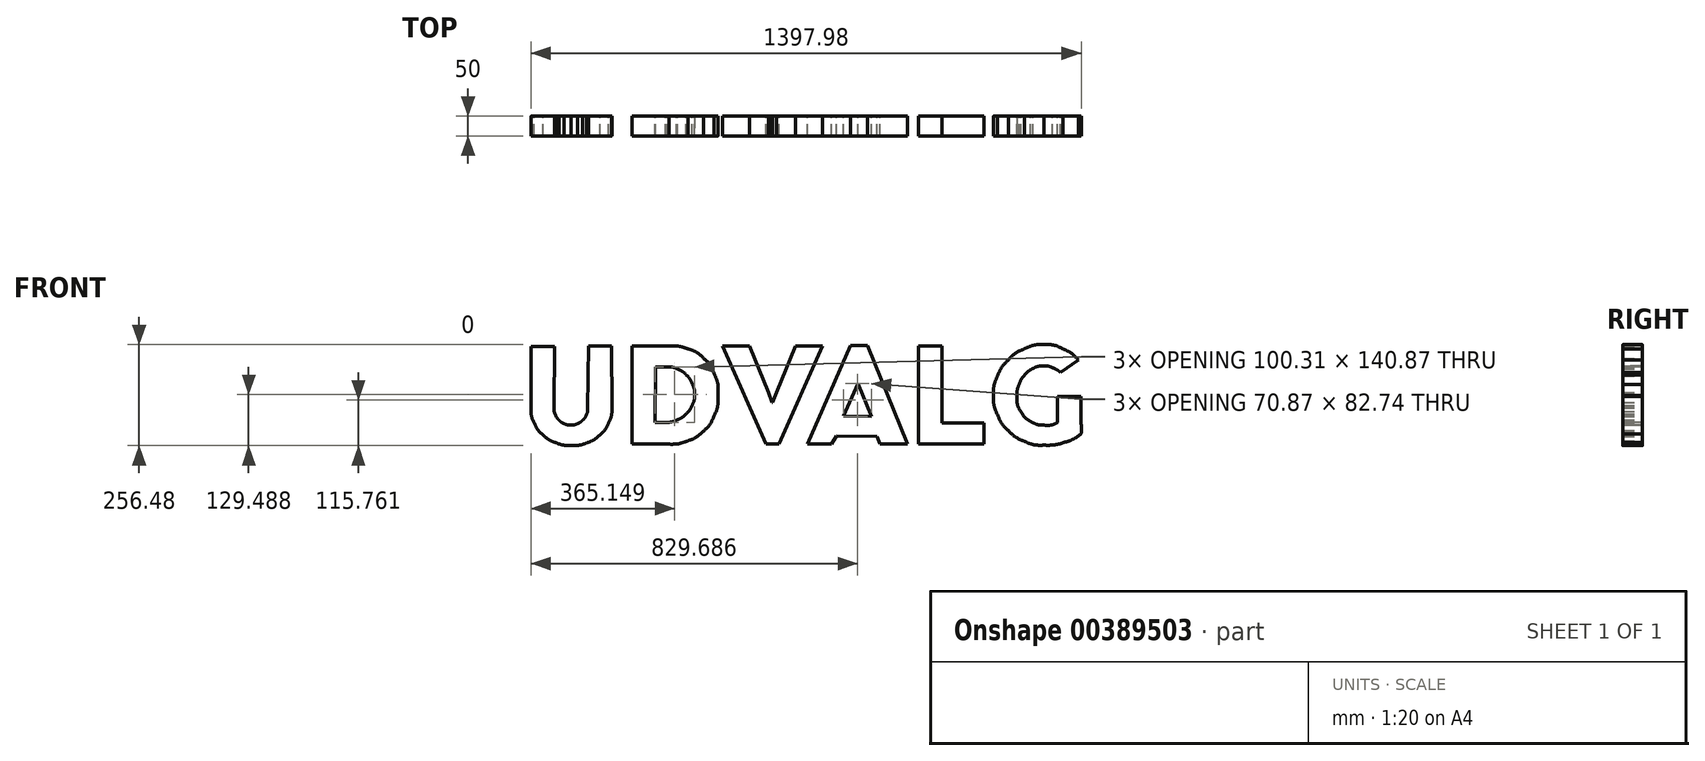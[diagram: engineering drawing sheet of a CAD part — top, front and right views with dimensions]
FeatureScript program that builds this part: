
annotation { "Feature Type Name" : "Feature", "Feature Type Description" : "" }
export const myFeature = defineFeature(function(context is Context, id is Id, definition is map)
    precondition{}
    {
        {
            var Q0;
            Q0=qCreatedBy(makeId("Front.planeOp"),FACE);
            var sketch = newSketch(context, id + "F0", { "sketchPlane" : qUnion([Q0])});
            skFitSpline(sketch, "E0", {"points": [v(-493.53, -31.17) * mm, v(-493.53, -45.27) * mm, v(-496.25, -58.25) * mm, v(-501.7, -70.12) * mm]});
            skFitSpline(sketch, "E1", {"points": [v(-501.7, -70.12) * mm, v(-506.89, -82) * mm, v(-514.18, -92.26) * mm, v(-523.58, -100.92) * mm]});
            skFitSpline(sketch, "E2", {"points": [v(-523.58, -100.92) * mm, v(-532.74, -109.33) * mm, v(-543.62, -116) * mm, v(-556.23, -120.95) * mm]});
            skFitSpline(sketch, "E3", {"points": [v(-556.23, -120.95) * mm, v(-568.6, -125.65) * mm, v(-581.83, -128) * mm, v(-595.93, -128) * mm]});
            skFitSpline(sketch, "E4", {"points": [v(-595.93, -128) * mm, v(-610.03, -128) * mm, v(-623.39, -125.65) * mm, v(-636, -120.95) * mm]});
            skFitSpline(sketch, "E5", {"points": [v(-636, -120.95) * mm, v(-648.37, -116.25) * mm, v(-659.25, -109.7) * mm, v(-668.65, -101.29) * mm]});
            skFitSpline(sketch, "E6", {"points": [v(-668.65, -101.29) * mm, v(-677.8, -92.88) * mm, v(-685.1, -82.86) * mm, v(-690.54, -71.24) * mm]});
            skFitSpline(sketch, "E7", {"points": [v(-690.54, -71.24) * mm, v(-695.99, -59.36) * mm, v(-698.7, -46.38) * mm, v(-698.7, -32.28) * mm]});
            skLineSegment(sketch, "E8", {"start": v(-553.27, 125.04) * mm, "end": v(-493.9, 125.04) * mm});
            skLineSegment(sketch, "E9", {"start": v(-493.9, 125.04) * mm, "end": v(-493.53, -31.17) * mm});
            skFitSpline(sketch, "E10", {"points": [v(-640.46, -33.02) * mm, v(-640.46, -38.96) * mm, v(-639.34, -44.52) * mm, v(-637.12, -49.72) * mm]});
            skFitSpline(sketch, "E11", {"points": [v(-637.12, -49.72) * mm, v(-634.9, -54.91) * mm, v(-631.8, -59.49) * mm, v(-627.84, -63.45) * mm]});
            skFitSpline(sketch, "E12", {"points": [v(-627.84, -63.45) * mm, v(-623.88, -67.4) * mm, v(-619.43, -70.5) * mm, v(-614.48, -72.72) * mm]});
            skFitSpline(sketch, "E13", {"points": [v(-614.48, -72.72) * mm, v(-609.29, -74.95) * mm, v(-603.72, -76.06) * mm, v(-597.79, -76.06) * mm]});
            skFitSpline(sketch, "E14", {"points": [v(-597.79, -76.06) * mm, v(-591.85, -76.06) * mm, v(-586.29, -74.95) * mm, v(-581.1, -72.72) * mm]});
            skFitSpline(sketch, "E15", {"points": [v(-581.1, -72.72) * mm, v(-575.9, -70.5) * mm, v(-571.32, -67.4) * mm, v(-567.36, -63.45) * mm]});
            skFitSpline(sketch, "E16", {"points": [v(-567.36, -63.45) * mm, v(-563.4, -59.49) * mm, v(-560.31, -54.91) * mm, v(-558.09, -49.72) * mm]});
            skFitSpline(sketch, "E17", {"points": [v(-558.09, -49.72) * mm, v(-555.86, -44.52) * mm, v(-554.75, -38.96) * mm, v(-554.75, -33.02) * mm]});
            skLineSegment(sketch, "E18", {"start": v(-698.7, -32.28) * mm, "end": v(-698.7, 123.92) * mm});
            skLineSegment(sketch, "E19", {"start": v(-698.7, 123.92) * mm, "end": v(-638.6, 123.92) * mm});
            skLineSegment(sketch, "E20", {"start": v(-638.6, 123.92) * mm, "end": v(-640.46, -33.02) * mm});
            skFitSpline(sketch, "E21", {"points": [v(-223.64, 0) * mm, v(-223.64, -19.79) * mm, v(-227.1, -37.47) * mm, v(-234.03, -53.06) * mm]});
            skFitSpline(sketch, "E22", {"points": [v(-234.03, -53.06) * mm, v(-240.71, -68.4) * mm, v(-249.86, -81.38) * mm, v(-261.49, -92.01) * mm]});
            skFitSpline(sketch, "E23", {"points": [v(-261.49, -92.01) * mm, v(-272.87, -102.65) * mm, v(-286.22, -110.81) * mm, v(-301.56, -116.5) * mm]});
            skFitSpline(sketch, "E24", {"points": [v(-301.56, -116.5) * mm, v(-316.9, -121.94) * mm, v(-333.22, -124.66) * mm, v(-350.53, -124.66) * mm]});
            skLineSegment(sketch, "E25", {"start": v(-554.75, -33.02) * mm, "end": v(-553.27, 125.04) * mm});
            skFitSpline(sketch, "E26", {"points": [v(-348.3, 125.04) * mm, v(-331.24, 125.04) * mm, v(-315.16, 122.44) * mm, v(-300.08, 117.24) * mm]});
            skFitSpline(sketch, "E27", {"points": [v(-300.08, 117.24) * mm, v(-284.74, 112.05) * mm, v(-271.5, 104.13) * mm, v(-260.38, 93.5) * mm]});
            skFitSpline(sketch, "E28", {"points": [v(-260.38, 93.5) * mm, v(-249, 83.1) * mm, v(-240.1, 70.12) * mm, v(-233.66, 54.54) * mm]});
            skFitSpline(sketch, "E29", {"points": [v(-233.66, 54.54) * mm, v(-226.98, 38.96) * mm, v(-223.64, 20.78) * mm, v(-223.64, 0) * mm]});
            skFitSpline(sketch, "E30", {"points": [v(-283.75, 1.48) * mm, v(-283.75, 11.13) * mm, v(-285.6, 20.16) * mm, v(-289.32, 28.57) * mm]});
            skFitSpline(sketch, "E31", {"points": [v(-289.32, 28.57) * mm, v(-293.03, 37.23) * mm, v(-298.1, 44.65) * mm, v(-304.53, 50.83) * mm]});
            skFitSpline(sketch, "E32", {"points": [v(-304.53, 50.83) * mm, v(-310.71, 57.26) * mm, v(-318.13, 62.33) * mm, v(-326.79, 66.04) * mm]});
            skFitSpline(sketch, "E33", {"points": [v(-326.79, 66.04) * mm, v(-335.45, 69.75) * mm, v(-344.6, 71.6) * mm, v(-354.24, 71.6) * mm]});
            skLineSegment(sketch, "E34", {"start": v(-350.53, -124.66) * mm, "end": v(-441.8, -124.66) * mm});
            skLineSegment(sketch, "E35", {"start": v(-441.8, -124.66) * mm, "end": v(-441.8, 125.04) * mm});
            skLineSegment(sketch, "E36", {"start": v(-441.8, 125.04) * mm, "end": v(-348.3, 125.04) * mm});
            skFitSpline(sketch, "E37", {"points": [v(-356.47, -69.01) * mm, v(-346.82, -69.01) * mm, v(-337.67, -67.16) * mm, v(-329.02, -63.45) * mm]});
            skFitSpline(sketch, "E38", {"points": [v(-329.02, -63.45) * mm, v(-320.11, -59.74) * mm, v(-312.32, -54.79) * mm, v(-305.64, -48.6) * mm]});
            skFitSpline(sketch, "E39", {"points": [v(-305.64, -48.6) * mm, v(-298.96, -42.17) * mm, v(-293.64, -34.63) * mm, v(-289.69, -25.97) * mm]});
            skFitSpline(sketch, "E40", {"points": [v(-289.69, -25.97) * mm, v(-285.73, -17.31) * mm, v(-283.75, -8.16) * mm, v(-283.75, 1.48) * mm]});
            skLineSegment(sketch, "E41", {"start": v(-354.24, 71.6) * mm, "end": v(-382.44, 71.6) * mm});
            skLineSegment(sketch, "E42", {"start": v(-382.44, 71.6) * mm, "end": v(-383.93, -69.01) * mm});
            skLineSegment(sketch, "E43", {"start": v(-383.93, -69.01) * mm, "end": v(-356.47, -69.01) * mm});
            skLineSegment(sketch, "E44", {"start": v(-95.45, 6.3) * mm, "end": v(-86.18, -18.55) * mm});
            skLineSegment(sketch, "E45", {"start": v(-86.18, -18.55) * mm, "end": v(-85.07, -18.55) * mm});
            skLineSegment(sketch, "E46", {"start": v(-85.07, -18.55) * mm, "end": v(-75.8, 6.3) * mm});
            skLineSegment(sketch, "E47", {"start": v(-75.8, 6.3) * mm, "end": v(-27.19, 124.66) * mm});
            skLineSegment(sketch, "E48", {"start": v(-27.19, 124.66) * mm, "end": v(41.82, 124.66) * mm});
            skLineSegment(sketch, "E49", {"start": v(41.82, 124.66) * mm, "end": v(-68.37, -124.3) * mm});
            skLineSegment(sketch, "E50", {"start": v(-68.37, -124.3) * mm, "end": v(-102.5, -124.3) * mm});
            skLineSegment(sketch, "E51", {"start": v(-102.5, -124.3) * mm, "end": v(-212.7, 124.66) * mm});
            skLineSegment(sketch, "E52", {"start": v(-212.7, 124.66) * mm, "end": v(-143.32, 124.66) * mm});
            skLineSegment(sketch, "E53", {"start": v(-143.32, 124.66) * mm, "end": v(-95.45, 6.3) * mm});
            skLineSegment(sketch, "E54", {"start": v(257.47, -124.66) * mm, "end": v(187.35, -124.66) * mm});
            skLineSegment(sketch, "E55", {"start": v(187.35, -124.66) * mm, "end": v(179.56, -104.63) * mm});
            skLineSegment(sketch, "E56", {"start": v(179.56, -104.63) * mm, "end": v(76.78, -103.89) * mm});
            skLineSegment(sketch, "E57", {"start": v(76.78, -103.89) * mm, "end": v(64.9, -124.66) * mm});
            skLineSegment(sketch, "E58", {"start": v(64.9, -124.66) * mm, "end": v(3.69, -124.66) * mm});
            skLineSegment(sketch, "E59", {"start": v(3.69, -124.66) * mm, "end": v(112.77, 125.4) * mm});
            skLineSegment(sketch, "E60", {"start": v(112.77, 125.4) * mm, "end": v(156.18, 125.4) * mm});
            skLineSegment(sketch, "E61", {"start": v(156.18, 125.4) * mm, "end": v(257.47, -124.66) * mm});
            skLineSegment(sketch, "E62", {"start": v(166.2, -53.8) * mm, "end": v(131.32, 28.94) * mm});
            skLineSegment(sketch, "E63", {"start": v(131.32, 28.94) * mm, "end": v(95.33, -52.69) * mm});
            skLineSegment(sketch, "E64", {"start": v(95.33, -52.69) * mm, "end": v(166.2, -53.8) * mm});
            skLineSegment(sketch, "E65", {"start": v(345.1, 125.04) * mm, "end": v(345.1, -70.5) * mm});
            skLineSegment(sketch, "E66", {"start": v(345.1, -70.5) * mm, "end": v(452.32, -70.5) * mm});
            skLineSegment(sketch, "E67", {"start": v(452.32, -70.5) * mm, "end": v(452.32, -124.66) * mm});
            skLineSegment(sketch, "E68", {"start": v(452.32, -124.66) * mm, "end": v(285.36, -124.66) * mm});
            skLineSegment(sketch, "E69", {"start": v(285.36, -124.66) * mm, "end": v(285.36, 124.66) * mm});
            skLineSegment(sketch, "E70", {"start": v(285.36, 124.66) * mm, "end": v(345.1, 125.04) * mm});
            skFitSpline(sketch, "E71", {"points": [v(698.7, -4.08) * mm, v(698.7, -67.16) * mm, v(698.58, -98.7) * mm, v(698.34, -98.7) * mm]});
            skFitSpline(sketch, "E72", {"points": [v(698.34, -98.7) * mm, v(684.98, -108.34) * mm, v(670.63, -115.51) * mm, v(655.3, -120.21) * mm]});
            skFitSpline(sketch, "E73", {"points": [v(655.3, -120.21) * mm, v(640.2, -124.91) * mm, v(622.9, -127.26) * mm, v(603.35, -127.26) * mm]});
            skFitSpline(sketch, "E74", {"points": [v(603.35, -127.26) * mm, v(586.04, -127.26) * mm, v(569.6, -123.92) * mm, v(554, -117.24) * mm]});
            skFitSpline(sketch, "E75", {"points": [v(554, -117.24) * mm, v(538.67, -110.57) * mm, v(525.2, -101.54) * mm, v(513.57, -90.16) * mm]});
            skFitSpline(sketch, "E76", {"points": [v(513.57, -90.16) * mm, v(501.94, -78.53) * mm, v(492.79, -65.05) * mm, v(486.1, -49.72) * mm]});
            skFitSpline(sketch, "E77", {"points": [v(486.1, -49.72) * mm, v(479.43, -34.38) * mm, v(476.1, -18.18) * mm, v(476.1, -1.11) * mm]});
            skFitSpline(sketch, "E78", {"points": [v(476.1, -1.11) * mm, v(476.1, 16.2) * mm, v(479.43, 32.65) * mm, v(486.1, 48.23) * mm]});
            skFitSpline(sketch, "E79", {"points": [v(486.1, 48.23) * mm, v(493.04, 63.82) * mm, v(502.31, 77.54) * mm, v(513.94, 89.42) * mm]});
            skFitSpline(sketch, "E80", {"points": [v(513.94, 89.42) * mm, v(525.56, 101.29) * mm, v(539.04, 110.69) * mm, v(554.38, 117.61) * mm]});
            skFitSpline(sketch, "E81", {"points": [v(554.38, 117.61) * mm, v(569.96, 124.54) * mm, v(586.4, 128) * mm, v(603.72, 128) * mm]});
            skFitSpline(sketch, "E82", {"points": [v(603.72, 128) * mm, v(621.53, 128) * mm, v(637.73, 124.42) * mm, v(652.33, 117.24) * mm]});
            skFitSpline(sketch, "E83", {"points": [v(652.33, 117.24) * mm, v(667.17, 110.32) * mm, v(680.28, 100.8) * mm, v(691.66, 88.67) * mm]});
            skLineSegment(sketch, "E84", {"start": v(638.97, -4.08) * mm, "end": v(698.7, -4.08) * mm});
            skFitSpline(sketch, "E85", {"points": [v(646.02, 57.5) * mm, v(639.84, 62.46) * mm, v(633.28, 66.41) * mm, v(626.36, 69.38) * mm]});
            skFitSpline(sketch, "E86", {"points": [v(626.36, 69.38) * mm, v(619.68, 72.35) * mm, v(612.01, 73.83) * mm, v(603.35, 73.83) * mm]});
            skFitSpline(sketch, "E87", {"points": [v(603.35, 73.83) * mm, v(593.7, 73.83) * mm, v(584.68, 71.73) * mm, v(576.27, 67.53) * mm]});
            skFitSpline(sketch, "E88", {"points": [v(576.27, 67.53) * mm, v(568.1, 63.32) * mm, v(561.06, 57.76) * mm, v(555.12, 50.83) * mm]});
            skFitSpline(sketch, "E89", {"points": [v(555.12, 50.83) * mm, v(549.18, 43.9) * mm, v(544.48, 35.87) * mm, v(541.02, 26.71) * mm]});
            skFitSpline(sketch, "E90", {"points": [v(541.02, 26.71) * mm, v(537.56, 17.8) * mm, v(535.83, 8.53) * mm, v(535.83, -1.11) * mm]});
            skFitSpline(sketch, "E91", {"points": [v(535.83, -1.11) * mm, v(535.83, -17.2) * mm, v(539.04, -30.67) * mm, v(545.47, -41.55) * mm]});
            skFitSpline(sketch, "E92", {"points": [v(545.47, -41.55) * mm, v(552.15, -52.44) * mm, v(560.44, -60.85) * mm, v(570.33, -66.78) * mm]});
            skFitSpline(sketch, "E93", {"points": [v(570.33, -66.78) * mm, v(580.47, -72.47) * mm, v(591.6, -75.69) * mm, v(603.72, -76.43) * mm]});
            skFitSpline(sketch, "E94", {"points": [v(603.72, -76.43) * mm, v(616.1, -76.93) * mm, v(627.84, -74.7) * mm, v(638.97, -69.75) * mm]});
            skLineSegment(sketch, "E95", {"start": v(691.66, 88.67) * mm, "end": v(646.02, 57.5) * mm});
            skLineSegment(sketch, "E96", {"start": v(638.97, -69.75) * mm, "end": v(638.97, -4.08) * mm});
            skSolve(sketch);
        }
        {
            var Q0;
            Q0 = qSketchRegion(id + "F0", true);
            extrude(context, id + "F1", {"entities" : qUnion([Q0]), "depth" : 50 * mm});
        }
    });
